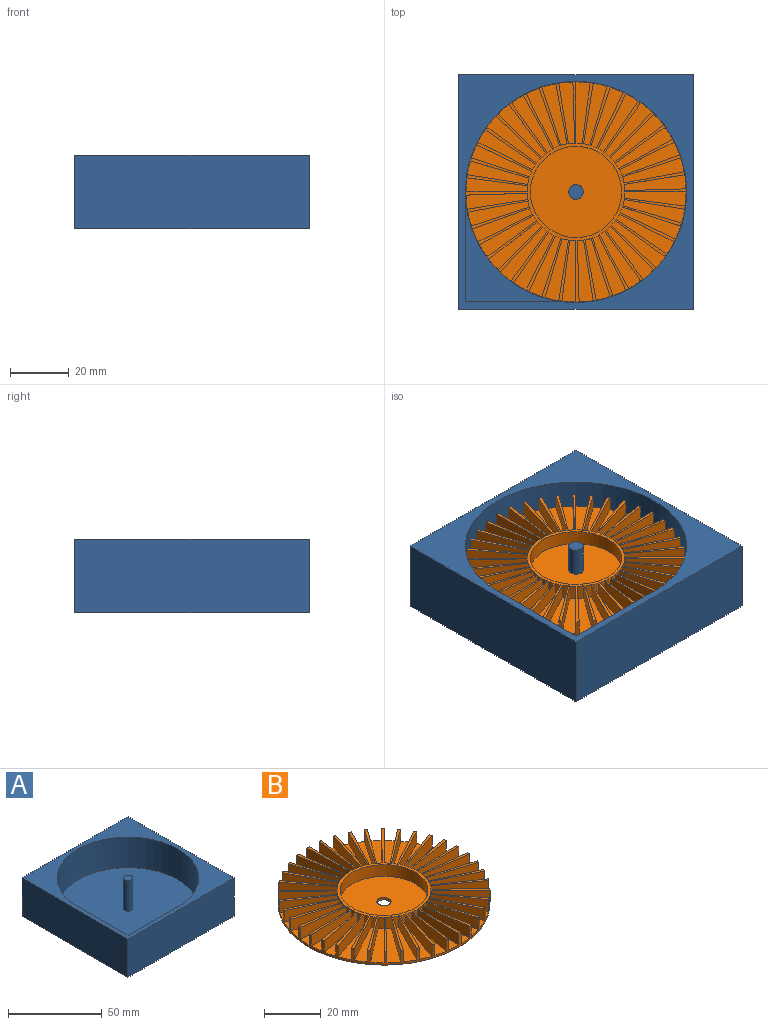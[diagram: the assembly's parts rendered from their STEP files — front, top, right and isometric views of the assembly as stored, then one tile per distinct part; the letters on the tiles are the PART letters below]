
ASSEMBLY  parts=2 mates=1
PART A: 14 faces, bbox 80x80x25 mm
  f0: cylinder r=37.72mm len=75.44mm, axis (0,0,-1), area 3719mm2, adj f5,f7,f8,f11
  f1: plane 80x25mm, normal (0,-1,0), area 2000mm2, adj f2,f4,f5,f6
  f2: plane 80x25mm, normal (1,0,0), area 2000mm2, adj f1,f3,f5,f6
  f3: plane 80x25mm, normal (0,1,0), area 2000mm2, adj f2,f4,f5,f6
  f4: plane 80x25mm, normal (-1,0,0), area 2000mm2, adj f1,f3,f5,f6
  f5: plane 80x80mm, normal (0,0,1), area 1639.8mm2, adj f0,f1,f2,f3,f4,f7,f8
  f6: plane 80x80mm, normal (0,0,-1), area 6400mm2, adj f1,f2,f3,f4
  f7: plane 33.41x22.5mm, normal (1,0,0), area 751.8mm2, adj f0,f5,f8,f9,f10
  f8: plane 33.41x22.5mm, normal (0,1,0), area 751.8mm2, adj f0,f5,f7,f9,f10
  f9: plane 33.41x33.41mm, normal (0,0,1), area 289.9mm2, adj f7,f8,f10
  f10: cylinder r=37.72mm len=33.41mm, axis (0,0,-1), area 127.7mm2, adj f7,f8,f9,f11
  f11: plane 75.44x75.44mm, normal (0,0,1), area 4450.7mm2, adj f0,f10,f13
  f12: plane 5x5mm, normal (0,0,1), area 19.6mm2, adj f13
  f13: cylinder r=2.5mm len=20mm, axis (0,0,-1), area 314.2mm2, adj f11,f12
PART B: 166 faces, bbox 75x75x6 mm
  f0: plane 31.11x31.11mm, normal (0,0,1), area 740.3mm2, adj f40,f86
  f1: plane 21.08x7.98mm, normal (0,0,1), area 72.8mm2, adj f41,f52,f89,f90
  f2: plane 20.64x10.94mm, normal (0,0,1), area 72.8mm2, adj f41,f51,f91,f92
  f3: plane 19.69x13.63mm, normal (0,0,1), area 72.8mm2, adj f41,f50,f93,f94
  f4: plane 18.25x15.99mm, normal (0,0,1), area 72.8mm2, adj f41,f49,f95,f96
  f5: plane 17.95x16.37mm, normal (0,0,1), area 72.8mm2, adj f41,f48,f97,f98
  f6: plane 19.47x14.08mm, normal (0,0,1), area 72.8mm2, adj f41,f47,f99,f100
  f7: plane 20.51x11.44mm, normal (0,0,1), area 72.8mm2, adj f41,f46,f101,f102
  f8: plane 21.06x5.4mm, normal (0,0,1), area 72.8mm2, adj f41,f44,f83,f105
  f9: plane 21.04x8.53mm, normal (0,0,1), area 72.8mm2, adj f41,f45,f103,f104
  f10: plane 21.01x4.82mm, normal (0,0,1), area 72.8mm2, adj f41,f84,f85,f107
  f11: plane 21.08x7.98mm, normal (0,0,1), area 72.8mm2, adj f41,f82,f106,f108
  f12: plane 20.64x10.94mm, normal (0,0,1), area 72.8mm2, adj f41,f81,f109,f110
  f13: plane 19.69x13.63mm, normal (0,0,1), area 72.8mm2, adj f41,f80,f111,f112
  f14: plane 18.25x15.99mm, normal (0,0,1), area 72.8mm2, adj f41,f79,f113,f114
  f15: plane 17.95x16.37mm, normal (0,0,1), area 72.8mm2, adj f41,f78,f115,f116
  f16: plane 19.47x14.08mm, normal (0,0,1), area 72.8mm2, adj f41,f77,f117,f118
  f17: plane 20.51x11.44mm, normal (0,0,1), area 72.8mm2, adj f41,f76,f119,f120
  f18: plane 21.04x8.53mm, normal (0,0,1), area 72.8mm2, adj f41,f75,f121,f122
  f19: plane 21.06x5.4mm, normal (0,0,1), area 72.8mm2, adj f41,f74,f123,f124
  f20: plane 21.01x4.82mm, normal (0,0,1), area 72.8mm2, adj f41,f73,f125,f126
  f21: plane 21.08x7.98mm, normal (0,0,1), area 72.8mm2, adj f41,f72,f127,f128
  f22: plane 20.64x10.94mm, normal (0,0,1), area 72.8mm2, adj f41,f71,f129,f130
  f23: plane 19.69x13.63mm, normal (0,0,1), area 72.8mm2, adj f41,f70,f131,f132
  f24: plane 18.25x15.99mm, normal (0,0,1), area 72.8mm2, adj f41,f69,f133,f134
  f25: plane 17.95x16.37mm, normal (0,0,1), area 72.8mm2, adj f41,f68,f135,f136
  f26: plane 19.47x14.08mm, normal (0,0,1), area 72.8mm2, adj f41,f67,f137,f138
  f27: plane 20.51x11.44mm, normal (0,0,1), area 72.8mm2, adj f41,f66,f139,f140
  f28: plane 21.04x8.53mm, normal (0,0,1), area 72.8mm2, adj f41,f65,f141,f142
  f29: plane 21.06x5.4mm, normal (0,0,1), area 72.8mm2, adj f41,f64,f143,f144
  f30: plane 21.01x4.82mm, normal (0,0,1), area 72.8mm2, adj f41,f63,f145,f146
  f31: plane 21.08x7.98mm, normal (0,0,1), area 72.8mm2, adj f41,f62,f147,f148
  f32: plane 20.64x10.94mm, normal (0,0,1), area 72.8mm2, adj f41,f61,f149,f150
  f33: plane 19.69x13.63mm, normal (0,0,1), area 72.8mm2, adj f41,f60,f151,f152
  f34: plane 18.25x15.99mm, normal (0,0,1), area 72.8mm2, adj f41,f59,f153,f154
  f35: plane 17.95x16.37mm, normal (0,0,1), area 72.8mm2, adj f41,f58,f155,f156
  f36: plane 19.47x14.08mm, normal (0,0,1), area 72.8mm2, adj f41,f57,f157,f158
  f37: plane 20.51x11.44mm, normal (0,0,1), area 72.8mm2, adj f41,f56,f159,f160
  f38: plane 21.04x8.53mm, normal (0,0,1), area 72.8mm2, adj f41,f55,f161,f162
  f39: plane 21.01x4.82mm, normal (0,0,1), area 72.8mm2, adj f41,f53,f88,f165
  f40: cylinder r=2.5mm len=5mm, axis (0,0,-1), area 15.7mm2, adj f0,f43
  f41: cylinder r=37.5mm len=75mm, axis (0,0,-1), area 446.8mm2, adj f1,f2,f3,f4,f5,f6,f7,f8
  f42: plane 21.06x5.4mm, normal (0,0,1), area 72.8mm2, adj f41,f54,f163,f164
  f43: plane 75x75mm, normal (0,0,-1), area 4398.2mm2, adj f40,f41
  f44: cylinder r=16.63mm len=5mm, axis (0,0,-1), area 10.7mm2, adj f8,f83,f87,f105
  f45: cylinder r=16.63mm len=5mm, axis (0,0,-1), area 10.7mm2, adj f9,f87,f103,f104
  f46: cylinder r=16.63mm len=5mm, axis (0,0,-1), area 10.7mm2, adj f7,f87,f101,f102
  f47: cylinder r=16.63mm len=5mm, axis (0,0,-1), area 10.7mm2, adj f6,f87,f99,f100
  f48: cylinder r=16.63mm len=5mm, axis (0,0,-1), area 10.7mm2, adj f5,f87,f97,f98
  f49: cylinder r=16.63mm len=5mm, axis (0,0,-1), area 10.7mm2, adj f4,f87,f95,f96
  f50: cylinder r=16.63mm len=5mm, axis (0,0,-1), area 10.7mm2, adj f3,f87,f93,f94
  f51: cylinder r=16.63mm len=5mm, axis (0,0,-1), area 10.7mm2, adj f2,f87,f91,f92
  f52: cylinder r=16.63mm len=5mm, axis (0,0,-1), area 10.7mm2, adj f1,f87,f89,f90
  f53: cylinder r=16.63mm len=5mm, axis (0,0,-1), area 10.7mm2, adj f39,f87,f88,f165
  f54: cylinder r=16.63mm len=5mm, axis (0,0,-1), area 10.7mm2, adj f42,f87,f163,f164
  f55: cylinder r=16.63mm len=5mm, axis (0,0,-1), area 10.7mm2, adj f38,f87,f161,f162
  f56: cylinder r=16.63mm len=5mm, axis (0,0,-1), area 10.7mm2, adj f37,f87,f159,f160
  f57: cylinder r=16.63mm len=5mm, axis (0,0,-1), area 10.7mm2, adj f36,f87,f157,f158
  f58: cylinder r=16.63mm len=5mm, axis (0,0,-1), area 10.7mm2, adj f35,f87,f155,f156
  f59: cylinder r=16.63mm len=5mm, axis (0,0,-1), area 10.7mm2, adj f34,f87,f153,f154
  f60: cylinder r=16.63mm len=5mm, axis (0,0,-1), area 10.7mm2, adj f33,f87,f151,f152
  f61: cylinder r=16.63mm len=5mm, axis (0,0,-1), area 10.7mm2, adj f32,f87,f149,f150
  f62: cylinder r=16.63mm len=5mm, axis (0,0,-1), area 10.7mm2, adj f31,f87,f147,f148
  f63: cylinder r=16.63mm len=5mm, axis (0,0,-1), area 10.7mm2, adj f30,f87,f145,f146
  f64: cylinder r=16.63mm len=5mm, axis (0,0,-1), area 10.7mm2, adj f29,f87,f143,f144
  f65: cylinder r=16.63mm len=5mm, axis (0,0,-1), area 10.7mm2, adj f28,f87,f141,f142
  f66: cylinder r=16.63mm len=5mm, axis (0,0,-1), area 10.7mm2, adj f27,f87,f139,f140
  f67: cylinder r=16.63mm len=5mm, axis (0,0,-1), area 10.7mm2, adj f26,f87,f137,f138
  f68: cylinder r=16.63mm len=5mm, axis (0,0,-1), area 10.7mm2, adj f25,f87,f135,f136
  f69: cylinder r=16.63mm len=5mm, axis (0,0,-1), area 10.7mm2, adj f24,f87,f133,f134
  f70: cylinder r=16.63mm len=5mm, axis (0,0,-1), area 10.7mm2, adj f23,f87,f131,f132
  f71: cylinder r=16.63mm len=5mm, axis (0,0,-1), area 10.7mm2, adj f22,f87,f129,f130
  f72: cylinder r=16.63mm len=5mm, axis (0,0,-1), area 10.7mm2, adj f21,f87,f127,f128
  f73: cylinder r=16.63mm len=5mm, axis (0,0,-1), area 10.7mm2, adj f20,f87,f125,f126
  f74: cylinder r=16.63mm len=5mm, axis (0,0,-1), area 10.7mm2, adj f19,f87,f123,f124
  f75: cylinder r=16.63mm len=5mm, axis (0,0,-1), area 10.7mm2, adj f18,f87,f121,f122
  f76: cylinder r=16.63mm len=5mm, axis (0,0,-1), area 10.7mm2, adj f17,f87,f119,f120
  f77: cylinder r=16.63mm len=5mm, axis (0,0,-1), area 10.7mm2, adj f16,f87,f117,f118
  f78: cylinder r=16.63mm len=5mm, axis (0,0,-1), area 10.7mm2, adj f15,f87,f115,f116
  f79: cylinder r=16.63mm len=5mm, axis (0,0,-1), area 10.7mm2, adj f14,f87,f113,f114
  f80: cylinder r=16.63mm len=5mm, axis (0,0,-1), area 10.7mm2, adj f13,f87,f111,f112
  f81: cylinder r=16.63mm len=5mm, axis (0,0,-1), area 10.7mm2, adj f12,f87,f109,f110
  f82: cylinder r=16.63mm len=5mm, axis (0,0,-1), area 10.7mm2, adj f11,f87,f106,f108
  f83: plane 20.86x5mm, normal (1,0.03,0), area 104.4mm2, adj f8,f41,f44,f87
  f84: cylinder r=16.63mm len=5mm, axis (0,0,-1), area 10.7mm2, adj f10,f85,f87,f107
  f85: plane 20.87x5mm, normal (-1,0,0), area 104.4mm2, adj f10,f41,f84,f87
  f86: cylinder r=15.55mm len=31.11mm, axis (0,0,-1), area 488.6mm2, adj f0,f87
  f87: plane 75x75mm, normal (0,0,1), area 745.1mm2, adj f41,f44,f45,f46,f47,f48,f49,f50
  f88: plane 20.7x5mm, normal (0.13,0.99,0), area 104.4mm2, adj f39,f41,f53,f87
  f89: plane 20.61x5mm, normal (-0.16,-0.99,0), area 104.4mm2, adj f1,f41,f52,f87
  f90: plane 20.02x5.89mm, normal (0.28,0.96,0), area 104.4mm2, adj f1,f41,f52,f87
  f91: plane 19.85x6.45mm, normal (-0.31,-0.95,0), area 104.4mm2, adj f2,f41,f51,f87
  f92: plane 18.86x8.95mm, normal (0.43,0.9,0), area 104.4mm2, adj f2,f41,f51,f87
  f93: plane 18.6x9.48mm, normal (-0.45,-0.89,0), area 104.4mm2, adj f3,f41,f50,f87
  f94: plane 17.22x11.79mm, normal (0.56,0.83,0), area 104.4mm2, adj f3,f41,f50,f87
  f95: plane 16.89x12.27mm, normal (-0.59,-0.81,0), area 104.4mm2, adj f4,f41,f49,f87
  f96: plane 15.17x14.34mm, normal (0.69,0.73,0), area 104.4mm2, adj f4,f41,f49,f87
  f97: plane 14.76x14.76mm, normal (-0.71,-0.71,0), area 104.4mm2, adj f5,f41,f48,f87
  f98: plane 16.53x12.74mm, normal (0.79,0.61,0), area 104.4mm2, adj f5,f41,f48,f87
  f99: plane 16.89x12.27mm, normal (-0.81,-0.59,0), area 104.4mm2, adj f6,f41,f47,f87
  f100: plane 18.32x10mm, normal (0.88,0.48,0), area 104.4mm2, adj f6,f41,f47,f87
  f101: plane 18.6x9.48mm, normal (-0.89,-0.45,0), area 104.4mm2, adj f7,f41,f46,f87
  f102: plane 19.66x7.01mm, normal (0.94,0.34,0), area 104.4mm2, adj f7,f41,f46,f87
  f103: plane 19.85x6.45mm, normal (-0.95,-0.31,0), area 104.4mm2, adj f9,f41,f45,f87
  f104: plane 20.51x5mm, normal (0.98,0.18,0), area 104.4mm2, adj f9,f41,f45,f87
  f105: plane 20.61x5mm, normal (-0.99,-0.16,0), area 104.4mm2, adj f8,f41,f44,f87
  f106: plane 20.61x5mm, normal (-0.99,0.16,0), area 104.4mm2, adj f11,f41,f82,f87
  f107: plane 20.7x5mm, normal (0.99,-0.13,0), area 104.4mm2, adj f10,f41,f84,f87
  f108: plane 20.02x5.89mm, normal (0.96,-0.28,0), area 104.4mm2, adj f11,f41,f82,f87
  f109: plane 19.85x6.45mm, normal (-0.95,0.31,0), area 104.4mm2, adj f12,f41,f81,f87
  f110: plane 18.86x8.95mm, normal (0.9,-0.43,0), area 104.4mm2, adj f12,f41,f81,f87
  f111: plane 18.6x9.48mm, normal (-0.89,0.45,0), area 104.4mm2, adj f13,f41,f80,f87
  f112: plane 17.22x11.79mm, normal (0.83,-0.56,0), area 104.4mm2, adj f13,f41,f80,f87
  f113: plane 16.89x12.27mm, normal (-0.81,0.59,0), area 104.4mm2, adj f14,f41,f79,f87
  f114: plane 15.17x14.34mm, normal (0.73,-0.69,0), area 104.4mm2, adj f14,f41,f79,f87
  f115: plane 14.76x14.76mm, normal (-0.71,0.71,0), area 104.4mm2, adj f15,f41,f78,f87
  f116: plane 16.53x12.74mm, normal (0.61,-0.79,0), area 104.4mm2, adj f15,f41,f78,f87
  f117: plane 16.89x12.27mm, normal (-0.59,0.81,0), area 104.4mm2, adj f16,f41,f77,f87
  f118: plane 18.32x10mm, normal (0.48,-0.88,0), area 104.4mm2, adj f16,f41,f77,f87
  f119: plane 18.6x9.48mm, normal (-0.45,0.89,0), area 104.4mm2, adj f17,f41,f76,f87
  f120: plane 19.66x7.01mm, normal (0.34,-0.94,0), area 104.4mm2, adj f17,f41,f76,f87
  f121: plane 19.85x6.45mm, normal (-0.31,0.95,0), area 104.4mm2, adj f18,f41,f75,f87
  f122: plane 20.51x5mm, normal (0.18,-0.98,0), area 104.4mm2, adj f18,f41,f75,f87
  f123: plane 20.61x5mm, normal (-0.16,0.99,0), area 104.4mm2, adj f19,f41,f74,f87
  f124: plane 20.86x5mm, normal (0.03,-1,0), area 104.4mm2, adj f19,f41,f74,f87
  f125: plane 20.87x5mm, normal (0,1,0), area 104.4mm2, adj f20,f41,f73,f87
  f126: plane 20.7x5mm, normal (-0.13,-0.99,0), area 104.4mm2, adj f20,f41,f73,f87
  f127: plane 20.61x5mm, normal (0.16,0.99,0), area 104.4mm2, adj f21,f41,f72,f87
  f128: plane 20.02x5.89mm, normal (-0.28,-0.96,0), area 104.4mm2, adj f21,f41,f72,f87
  f129: plane 19.85x6.45mm, normal (0.31,0.95,0), area 104.4mm2, adj f22,f41,f71,f87
  f130: plane 18.86x8.95mm, normal (-0.43,-0.9,0), area 104.4mm2, adj f22,f41,f71,f87
  f131: plane 18.6x9.48mm, normal (0.45,0.89,0), area 104.4mm2, adj f23,f41,f70,f87
  f132: plane 17.22x11.79mm, normal (-0.56,-0.83,0), area 104.4mm2, adj f23,f41,f70,f87
  f133: plane 16.89x12.27mm, normal (0.59,0.81,0), area 104.4mm2, adj f24,f41,f69,f87
  f134: plane 15.17x14.34mm, normal (-0.69,-0.73,0), area 104.4mm2, adj f24,f41,f69,f87
  f135: plane 14.76x14.76mm, normal (0.71,0.71,0), area 104.4mm2, adj f25,f41,f68,f87
  f136: plane 16.53x12.74mm, normal (-0.79,-0.61,0), area 104.4mm2, adj f25,f41,f68,f87
  f137: plane 16.89x12.27mm, normal (0.81,0.59,0), area 104.4mm2, adj f26,f41,f67,f87
  f138: plane 18.32x10mm, normal (-0.88,-0.48,0), area 104.4mm2, adj f26,f41,f67,f87
  f139: plane 18.6x9.48mm, normal (0.89,0.45,0), area 104.4mm2, adj f27,f41,f66,f87
  f140: plane 19.66x7.01mm, normal (-0.94,-0.34,0), area 104.4mm2, adj f27,f41,f66,f87
  f141: plane 19.85x6.45mm, normal (0.95,0.31,0), area 104.4mm2, adj f28,f41,f65,f87
  f142: plane 20.51x5mm, normal (-0.98,-0.18,0), area 104.4mm2, adj f28,f41,f65,f87
  f143: plane 20.61x5mm, normal (0.99,0.16,0), area 104.4mm2, adj f29,f41,f64,f87
  f144: plane 20.86x5mm, normal (-1,-0.03,0), area 104.4mm2, adj f29,f41,f64,f87
  f145: plane 20.87x5mm, normal (1,0,0), area 104.4mm2, adj f30,f41,f63,f87
  f146: plane 20.7x5mm, normal (-0.99,0.13,0), area 104.4mm2, adj f30,f41,f63,f87
  f147: plane 20.61x5mm, normal (0.99,-0.16,0), area 104.4mm2, adj f31,f41,f62,f87
  f148: plane 20.02x5.89mm, normal (-0.96,0.28,0), area 104.4mm2, adj f31,f41,f62,f87
  f149: plane 19.85x6.45mm, normal (0.95,-0.31,0), area 104.4mm2, adj f32,f41,f61,f87
  f150: plane 18.86x8.95mm, normal (-0.9,0.43,0), area 104.4mm2, adj f32,f41,f61,f87
  f151: plane 18.6x9.48mm, normal (0.89,-0.45,0), area 104.4mm2, adj f33,f41,f60,f87
  f152: plane 17.22x11.79mm, normal (-0.83,0.56,0), area 104.4mm2, adj f33,f41,f60,f87
  f153: plane 16.89x12.27mm, normal (0.81,-0.59,0), area 104.4mm2, adj f34,f41,f59,f87
  f154: plane 15.17x14.34mm, normal (-0.73,0.69,0), area 104.4mm2, adj f34,f41,f59,f87
  f155: plane 14.76x14.76mm, normal (0.71,-0.71,0), area 104.4mm2, adj f35,f41,f58,f87
  f156: plane 16.53x12.74mm, normal (-0.61,0.79,0), area 104.4mm2, adj f35,f41,f58,f87
  f157: plane 16.89x12.27mm, normal (0.59,-0.81,0), area 104.4mm2, adj f36,f41,f57,f87
  f158: plane 18.32x10mm, normal (-0.48,0.88,0), area 104.4mm2, adj f36,f41,f57,f87
  f159: plane 18.6x9.48mm, normal (0.45,-0.89,0), area 104.4mm2, adj f37,f41,f56,f87
  f160: plane 19.66x7.01mm, normal (-0.34,0.94,0), area 104.4mm2, adj f37,f41,f56,f87
  f161: plane 19.85x6.45mm, normal (0.31,-0.95,0), area 104.4mm2, adj f38,f41,f55,f87
  f162: plane 20.51x5mm, normal (-0.18,0.98,0), area 104.4mm2, adj f38,f41,f55,f87
  f163: plane 20.61x5mm, normal (0.16,-0.99,0), area 104.4mm2, adj f41,f42,f54,f87
  f164: plane 20.86x5mm, normal (-0.03,1,0), area 104.4mm2, adj f41,f42,f54,f87
  f165: plane 20.87x5mm, normal (0,-1,0), area 104.4mm2, adj f39,f41,f53,f87
PLACE A t=(-37.23,0.92,7.3)mm
PLACE B t=(-37.23,0.92,21.3)mm
MATE revolute A.f13 <-> B.f86  axis (0,0,-1) through (-37.23,0.92,22.3)mm
